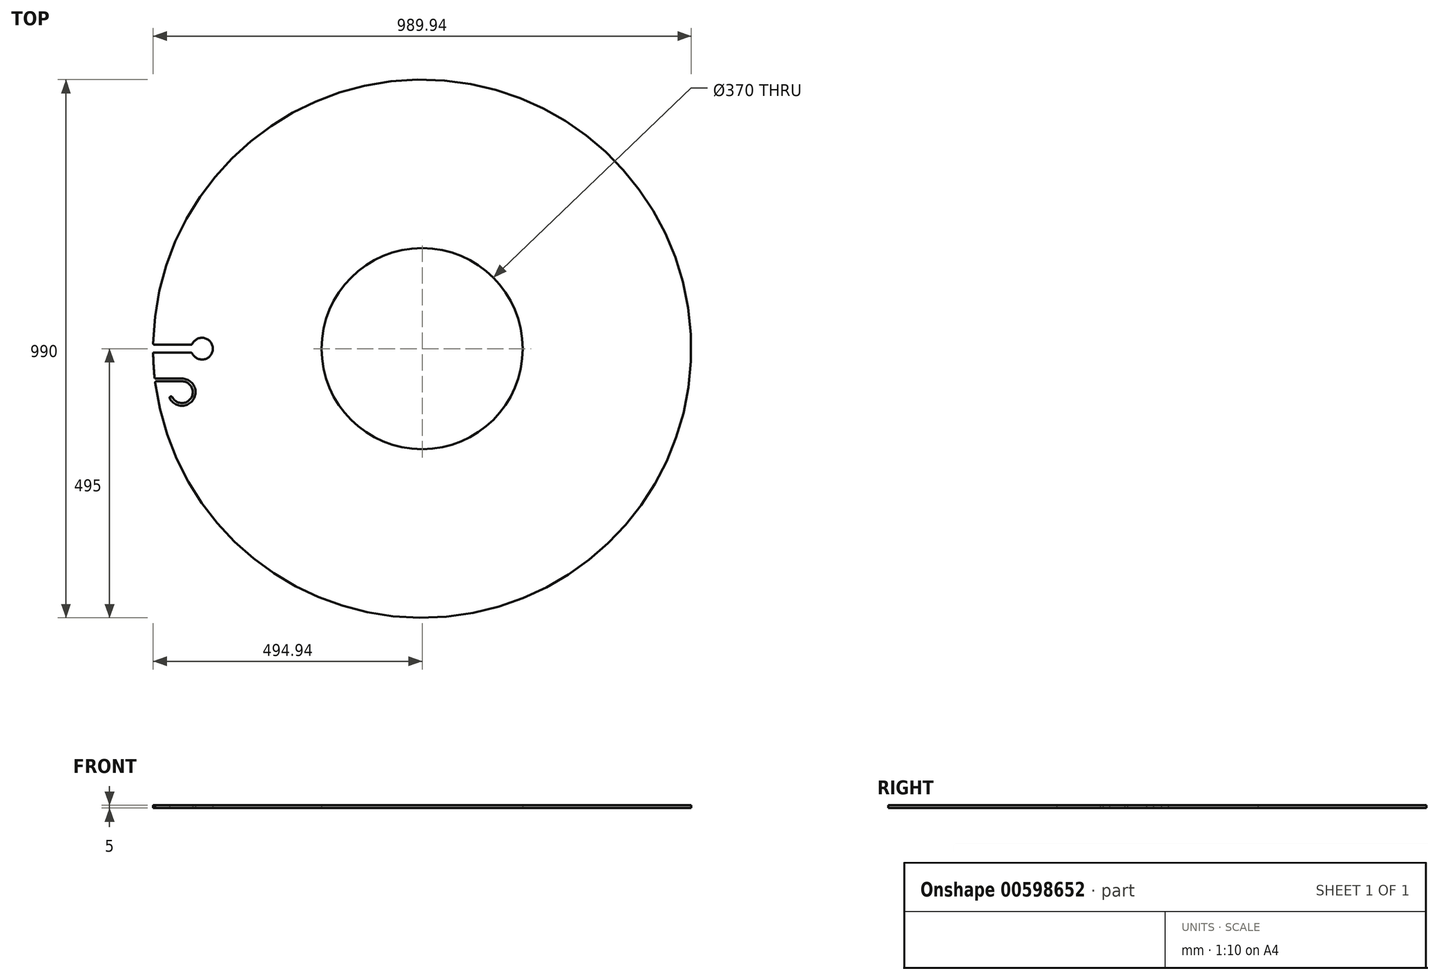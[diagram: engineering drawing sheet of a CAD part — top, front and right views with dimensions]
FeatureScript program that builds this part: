
annotation { "Feature Type Name" : "Feature", "Feature Type Description" : "" }
export const myFeature = defineFeature(function(context is Context, id is Id, definition is map)
    precondition{}
    {
        {
            var Q0;
            Q0=qCreatedBy(makeId("Top.planeOp"),FACE);
            var sketch = newSketch(context, id + "F0", { "sketchPlane" : qUnion([Q0])});
            skCircle(sketch, "E0", {"center": v(0, 0) * mm, "radius": 495 * mm});
            skCircle(sketch, "E1", {"center": v(0, 0) * mm, "radius": 185 * mm});
            skLineSegment(sketch, "E2", {"start": v(0, 0) * mm, "end": v(-495, 0) * mm, "construction": true});
            skArc(sketch, "E3", {"start": v(-423.04, -8.64) * mm, "mid": v(-385, 0) * mm, "end": v(-423.04, 8.64) * mm});
            skLineSegment(sketch, "E4", {"start": v(-494.94, 7.5) * mm, "end": v(-424.84, 7.5) * mm});
            skLineSegment(sketch, "E5", {"start": v(-494.94, -7.5) * mm, "end": v(-424.84, -7.5) * mm});
            skLineSegment(sketch, "E6.MirrorCS", {"start": v(-491.35, -60) * mm, "end": v(-441.93, -60) * mm});
            skLineSegment(sketch, "E7.MirrorCS", {"start": v(-491.93, -55) * mm, "end": v(-441.93, -55) * mm});
            skArc(sketch, "E8.MirrorCS", {"start": v(-441.93, -55) * mm, "mid": v(-420.59, -93.01) * mm, "end": v(-464.16, -91.45) * mm});
            skArc(sketch, "E9.MirrorCS", {"start": v(-441.93, -60) * mm, "mid": v(-424.86, -90.41) * mm, "end": v(-459.71, -89.16) * mm});
            skArc(sketch, "E10.MirrorCS", {"start": v(-464.16, -91.45) * mm, "mid": v(-463.08, -88.09) * mm, "end": v(-459.71, -89.16) * mm});
            skCircle(sketch, "E11", {"center": v(-405, 0) * mm, "radius": 50 * mm, "construction": true});
            skCircle(sketch, "E12", {"center": v(-461.93, -90.3) * mm, "radius": 4 * mm, "construction": true});
            skPoint(sketch, "E13.visualSharp", {"position": v(-423.54, 7.5) * mm});
            skArc(sketch, "E13.filletArc", {"start": v(-424.84, 7.5) * mm, "mid": v(-423.78, 7.8) * mm, "end": v(-423.04, 8.64) * mm});
            skPoint(sketch, "E14.visualSharp", {"position": v(-423.54, -7.5) * mm});
            skArc(sketch, "E14.filletArc", {"start": v(-423.04, -8.64) * mm, "mid": v(-423.78, -7.8) * mm, "end": v(-424.84, -7.5) * mm});
            skSolve(sketch);
        }
        {
            var Q0;
            Q0=qCreatedBy(makeId("Front.planeOp"),FACE);
            var sketch = newSketch(context, id + "F1", { "sketchPlane" : qUnion([Q0])});
            skLineSegment(sketch, "E15", {"start": v(0, 40) * mm, "end": v(0, -40) * mm, "construction": true});
            skSolve(sketch);
        }
        {
            var Q0;
            Q0=makeQuery(id+"F0.imprint","IMPRINT",FACE,{"disambiguationData":[TD([[makeQuery(id+"F0.imprint","IMPRINT",EDGE,{"derivedFrom":sQuery(id+"F0.wireOp",EDGE,"E1")}),-1.0]])]});
            var Q1;
            {var subQ0=sQuery(id+"F0.wireOp",EDGE,"E3");var subQ1=makeQuery(id+"F0.imprint","INTERSECT",VERTEX,{"derivedFrom":[subQ0,sQuery(id+"F0.wireOp",EDGE,"E4")]});Q1=makeQuery(id+"F0.imprint","IMPRINT",FACE,{"disambiguationData":[TD([[makeQuery(id+"F0.imprint","IMPRINT",EDGE,{"disambiguationData":[TD([[subQ1,-1.0]])],"derivedFrom":subQ0}),1.0]])]});}
            var Q2;
            {var subQ0=sQuery(id+"F0.wireOp",EDGE,"E4");Q2=makeQuery(id+"F0.imprint","IMPRINT",FACE,{"disambiguationData":[TD([[makeQuery(id+"F0.imprint","IMPRINT",EDGE,{"derivedFrom":subQ0}),-1.0]])]});}
            var Q3;
            {var subQ1=sQuery(id+"F0.wireOp",EDGE,"E6.MirrorCS");Q3=makeQuery(id+"F0.imprint","IMPRINT",FACE,{"disambiguationData":[TD([[makeQuery(id+"F0.imprint","IMPRINT",EDGE,{"derivedFrom":subQ1}),1.0]])]});}
            extrude(context, id + "F2", {"entities" : qUnion([Q0, Q1, Q2, Q3]), "depth" : 5 * mm, "offsetDistance" : 25 * mm});
        }
        {
            var Q0;
            {var subQ0=sQuery(id+"F0.wireOp",EDGE,"E3");var subQ1=makeQuery(id+"F0.imprint","INTERSECT",VERTEX,{"derivedFrom":[subQ0,sQuery(id+"F0.wireOp",EDGE,"E4")]});Q0=makeQuery(id+"F0.imprint","IMPRINT",FACE,{"disambiguationData":[TD([[makeQuery(id+"F0.imprint","IMPRINT",EDGE,{"disambiguationData":[TD([[subQ1,-1.0]])],"derivedFrom":subQ0}),1.0]])]});}
            var Q1;
            {var subQ0=sQuery(id+"F0.wireOp",EDGE,"E4");Q1=makeQuery(id+"F0.imprint","IMPRINT",FACE,{"disambiguationData":[TD([[makeQuery(id+"F0.imprint","IMPRINT",EDGE,{"derivedFrom":subQ0}),-1.0]])]});}
            var Q2;
            {var subQ1=sQuery(id+"F0.wireOp",EDGE,"E6.MirrorCS");Q2=makeQuery(id+"F0.imprint","IMPRINT",FACE,{"disambiguationData":[TD([[makeQuery(id+"F0.imprint","IMPRINT",EDGE,{"derivedFrom":subQ1}),1.0]])]});}
            var Q3;
            Q3=makeQuery(id+"F2.opExtrude","CAP_FACE",FACE,{"disambiguationData":[OSD([sQuery(id+"F0.wireOp",EDGE,"E0"),sQuery(id+"F0.wireOp",EDGE,"E1")])],"isStart":false});
            extrude(context, id + "F3", {"entities" : qUnion([Q0, Q1, Q2]), "operationType" : NewBodyOperationType.REMOVE, "endBound" : BoundingType.UP_TO_SURFACE, "depth" : 25 * mm, "endBoundEntityFace" : qUnion([Q3]), "offsetDistance" : 25 * mm});
        }
        {
            var Q0;
            Q0=makeQuery(id+"F3.boolean.opBoolean","COPY",EDGE,{"derivedFrom":makeQuery(id+"F3.opExtrude","SWEPT_EDGE",EDGE,{"disambiguationData":[OSD([sQuery(id+"F0.wireOp",EDGE,"E0"),sQuery(id+"F0.wireOp",EDGE,"E5")])]})});
            var Q1;
            Q1=makeQuery(id+"F3.boolean.opBoolean","COPY",EDGE,{"derivedFrom":makeQuery(id+"F3.opExtrude","SWEPT_EDGE",EDGE,{"disambiguationData":[OSD([sQuery(id+"F0.wireOp",EDGE,"E0"),sQuery(id+"F0.wireOp",EDGE,"E4")])]})});
            var Q2;
            Q2=makeQuery(id+"F3.boolean.opBoolean","COPY",EDGE,{"derivedFrom":makeQuery(id+"F3.opExtrude","SWEPT_EDGE",EDGE,{"disambiguationData":[OSD([sQuery(id+"F0.wireOp",EDGE,"E0"),sQuery(id+"F0.wireOp",EDGE,"E7.MirrorCS")])]})});
            var Q3;
            Q3=makeQuery(id+"F3.boolean.opBoolean","COPY",EDGE,{"derivedFrom":makeQuery(id+"F3.opExtrude","SWEPT_EDGE",EDGE,{"disambiguationData":[OSD([sQuery(id+"F0.wireOp",EDGE,"E0"),sQuery(id+"F0.wireOp",EDGE,"E6.MirrorCS")])]})});
            fillet(context, id + "F4", {"entities" : qUnion([Q0, Q1, Q2, Q3]), "radius" : 2 * mm, "tangentPropagation" : true, "allowEdgeOverflow" : false});
        }
    });
